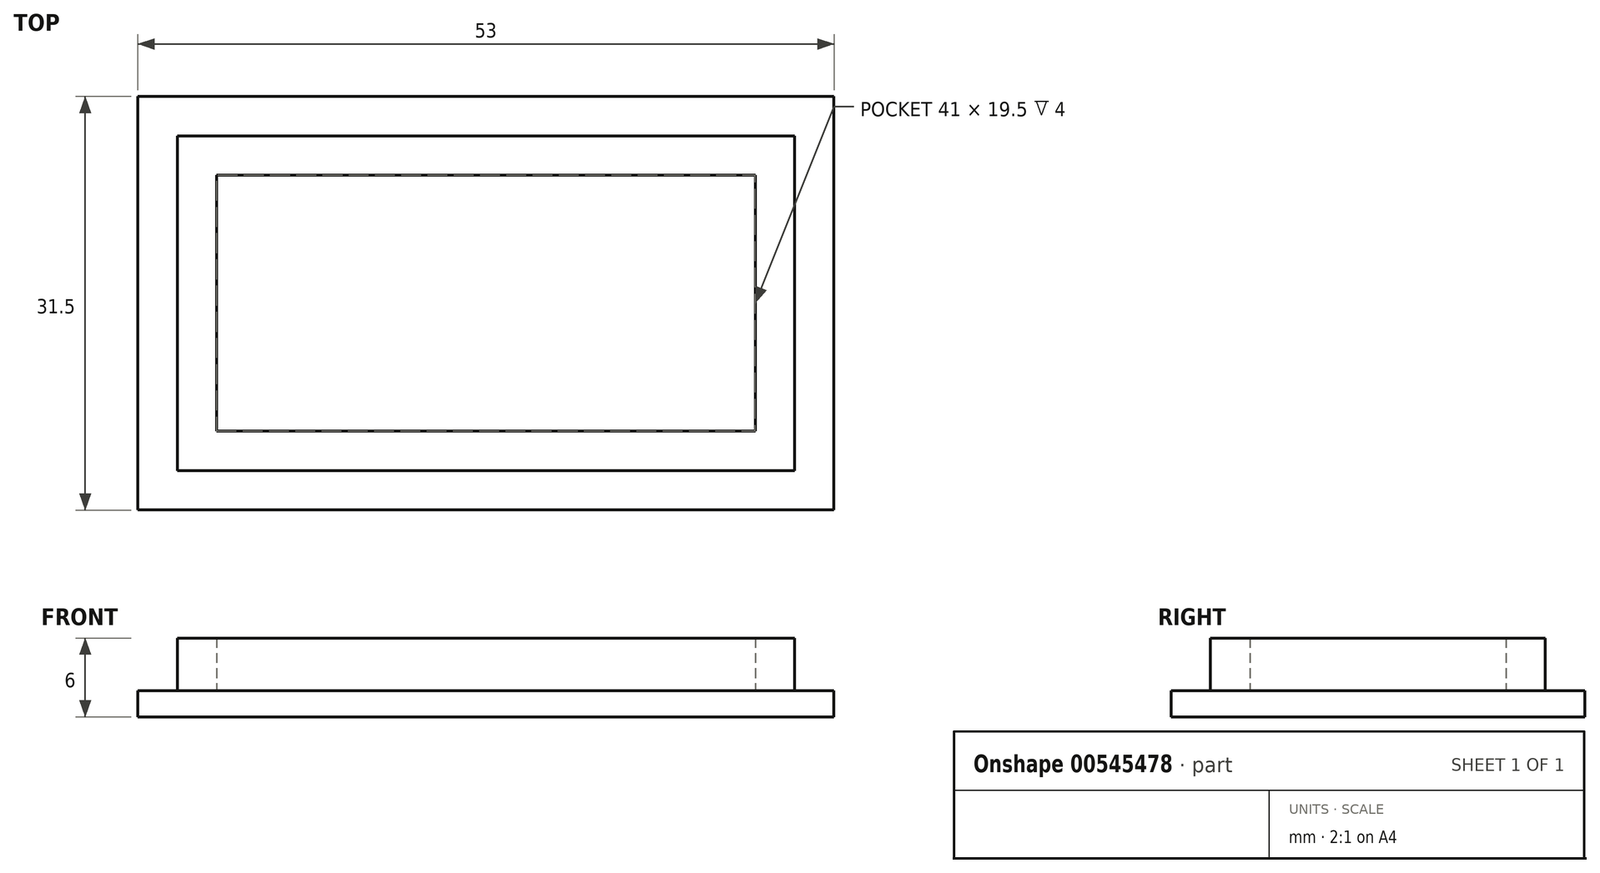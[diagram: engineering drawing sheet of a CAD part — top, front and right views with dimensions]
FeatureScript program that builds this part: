
annotation { "Feature Type Name" : "Feature", "Feature Type Description" : "" }
export const myFeature = defineFeature(function(context is Context, id is Id, definition is map)
    precondition{}
    {
        {
            var Q0;
            Q0=qCreatedBy(makeId("Top.planeOp"),FACE);
            var sketch = newSketch(context, id + "F0", { "sketchPlane" : qUnion([Q0])});
            skLineSegment(sketch, "E0.bottom", {"start": v(-28.4, 1.64) * mm, "end": v(18.6, 1.64) * mm});
            skLineSegment(sketch, "E0.top", {"start": v(-28.4, -23.86) * mm, "end": v(18.6, -23.86) * mm});
            skLineSegment(sketch, "E0.left", {"start": v(-28.4, 1.64) * mm, "end": v(-28.4, -23.86) * mm});
            skLineSegment(sketch, "E0.right", {"start": v(18.6, 1.64) * mm, "end": v(18.6, -23.86) * mm});
            skLineSegment(sketch, "E1.bottom", {"start": v(-25.4, -20.86) * mm, "end": v(15.6, -20.86) * mm});
            skLineSegment(sketch, "E1.top", {"start": v(-25.4, -1.36) * mm, "end": v(15.6, -1.36) * mm});
            skLineSegment(sketch, "E1.left", {"start": v(-25.4, -20.86) * mm, "end": v(-25.4, -1.36) * mm});
            skLineSegment(sketch, "E1.right", {"start": v(15.6, -20.86) * mm, "end": v(15.6, -1.36) * mm});
            skSolve(sketch);
        }
        {
            var Q0;
            Q0 = qSketchRegion(id + "F0", true);
            extrude(context, id + "F1", {"entities" : qUnion([Q0]), "depth" : 4 * mm, "offsetDistance" : 25 * mm});
        }
        {
            var Q0;
            Q0=makeQuery(id+"F1.opExtrude","CAP_FACE",FACE,{"disambiguationData":[OSD([sQuery(id+"F0.wireOp",EDGE,"E0.bottom"),sQuery(id+"F0.wireOp",EDGE,"E0.top"),sQuery(id+"F0.wireOp",EDGE,"E0.left"),sQuery(id+"F0.wireOp",EDGE,"E0.right"),sQuery(id+"F0.wireOp",EDGE,"E1.bottom"),sQuery(id+"F0.wireOp",EDGE,"E1.top"),sQuery(id+"F0.wireOp",EDGE,"E1.left"),sQuery(id+"F0.wireOp",EDGE,"E1.right")])],"isStart":true});
            var sketch = newSketch(context, id + "F2", { "sketchPlane" : qUnion([Q0])});
            skLineSegment(sketch, "E2.bottom", {"start": v(-31.4, 26.86) * mm, "end": v(21.6, 26.86) * mm});
            skLineSegment(sketch, "E2.top", {"start": v(-31.4, -4.64) * mm, "end": v(21.6, -4.64) * mm});
            skLineSegment(sketch, "E2.left", {"start": v(-31.4, 26.86) * mm, "end": v(-31.4, -4.64) * mm});
            skLineSegment(sketch, "E2.right", {"start": v(21.6, 26.86) * mm, "end": v(21.6, -4.64) * mm});
            skSolve(sketch);
        }
        {
            var Q0;
            Q0=makeQuery(id+"F2.imprint","IMPRINT",FACE,{"disambiguationData":[TD([[makeQuery(id+"F2.imprint","IMPRINT",EDGE,{"derivedFrom":sQuery(id+"F2.wireOp",EDGE,"E2.bottom")}),-1.0]])]});
            var Q1;
            Q1=makeQuery(id+"F2.imprint","IMPRINT",FACE,{"disambiguationData":[TD([[makeQuery(id+"F2.imprint","IMPRINT",EDGE,{"derivedFrom":makeQuery(id+"F1.opExtrude","CAP_EDGE",EDGE,{"disambiguationData":[OSD([sQuery(id+"F0.wireOp",EDGE,"E0.bottom")])],"isStart":true})}),1.0]])]});
            var Q2;
            Q2=makeQuery(id+"F2.imprint","IMPRINT",FACE,{"disambiguationData":[TD([[makeQuery(id+"F2.imprint","IMPRINT",EDGE,{"derivedFrom":makeQuery(id+"F1.opExtrude","CAP_EDGE",EDGE,{"disambiguationData":[OSD([sQuery(id+"F0.wireOp",EDGE,"E1.bottom")])],"isStart":true})}),-1.0]])]});
            extrude(context, id + "F3", {"entities" : qUnion([Q0, Q1, Q2]), "operationType" : NewBodyOperationType.ADD, "depth" : 2 * mm, "offsetDistance" : 25 * mm});
        }
    });
